# Revit family: LTV8DM
name_source: partatom
category: Lighting Fixtures
units: mm (PartAtom-declared; Revit-internal decimal feet)

## family parameters
Cut with Voids When Loaded = No
Host = Face
Light Source = Yes
OmniClass Number = 23.80.70.14.14
OmniClass Title = Exterior Floodlights
Part Type = Normal
Room Calculation Point = No
Round Connector Dimension = Use Diameter
Shared = No

## types (3) — shared parameters
Apparent Load = 0 VA
Color Filter = 16777215
Default Elevation = 48.000"
Description = Directional marker for drive way applications or path finding
Dimming Lamp Color Temperature Shift = <None>
Emit Shape Visible in Rendering = No
Emit from Circle Diameter = 4.000"
Glass = White Glass
Housing Material = Powdercoat - Bronze
Lamp = LED
Load Classification = Lighting
Manufacturer = Kim Lighting
Model = Lightvault® LTV8DM Directional Marker
Photometric Notes = More IES files download on Photometric Web Link
Power Factor = 1
Tilt Angle = 90.00°
URL = https://www.currentlighting.com
Voltage = 120 V

## per-type parameters (varying)
| type | Fixture | Nominal Watts | Photometric Web File |
| LTV81DM | LTV8D : LTV81DM | 31 W | ltv81dm-24l3k.ies |
| LTV82DM | LTV8D : LTV82DM | 23 W | ltv82dm-18l3k.ies |
| LTV83DM | LTV8D : LTV83DM | 14 W | ltv83dm-12l3k.ies |

## geometry (parser evidence)
native form markers: Blend x2, Sweep x5
no freeform markers — native parametric forms only
